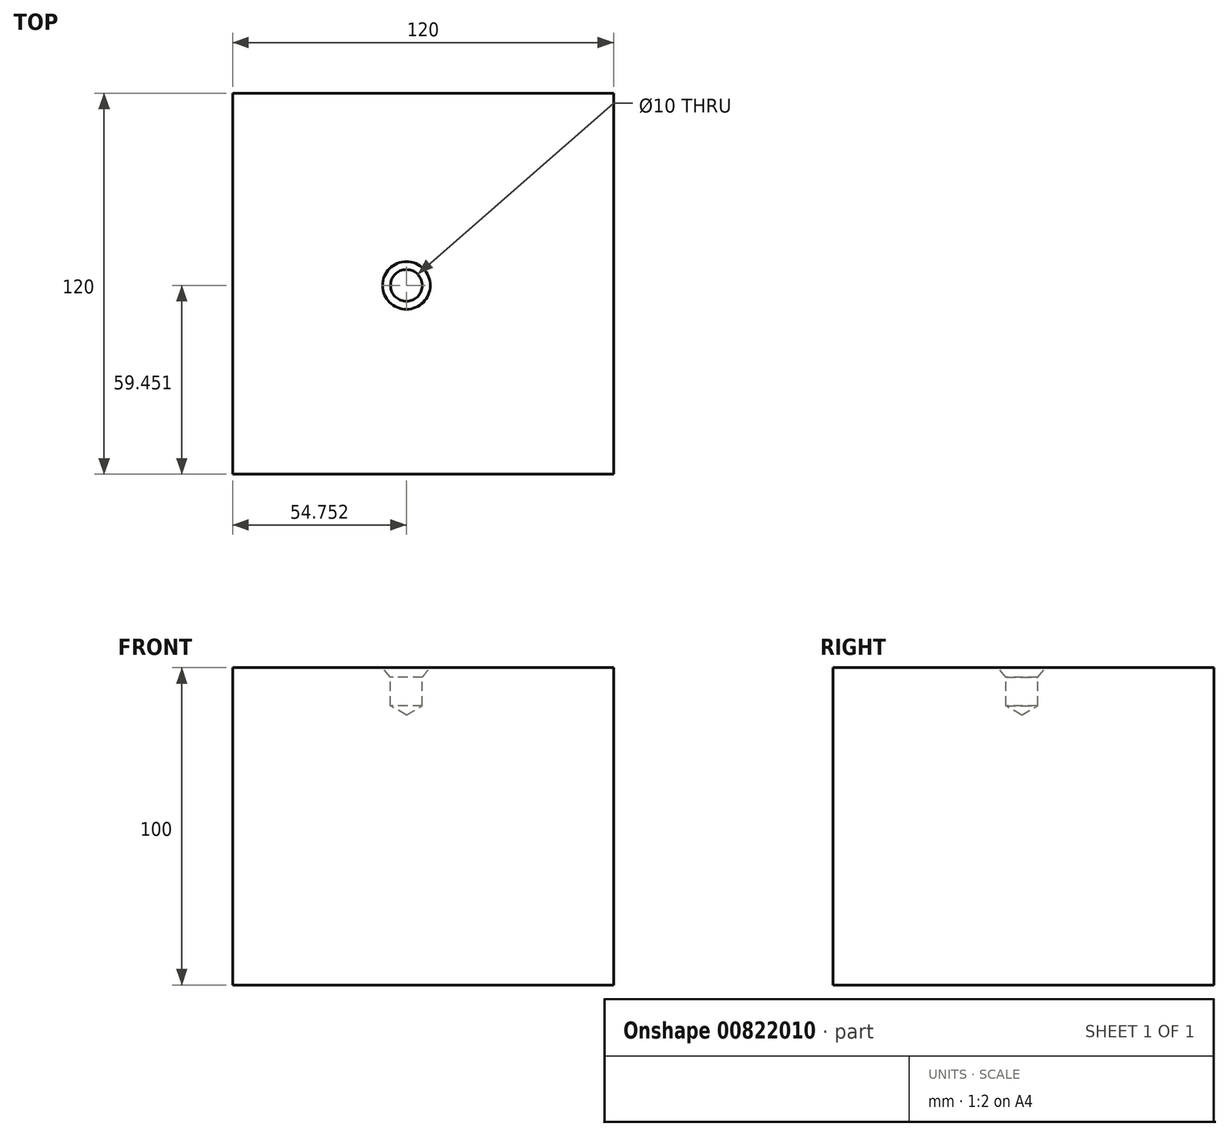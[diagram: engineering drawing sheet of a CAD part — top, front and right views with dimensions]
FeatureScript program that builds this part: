
annotation { "Feature Type Name" : "Feature", "Feature Type Description" : "" }
export const myFeature = defineFeature(function(context is Context, id is Id, definition is map)
    precondition{}
    {
        {
            var Q0;
            Q0=qCreatedBy(makeId("Top.planeOp"),FACE);
            var sketch = newSketch(context, id + "F0", { "sketchPlane" : qUnion([Q0])});
            skLineSegment(sketch, "E0.bottom", {"start": v(-65.58, -51.94) * mm, "end": v(54.42, -51.94) * mm});
            skLineSegment(sketch, "E0.top", {"start": v(-65.58, 68.06) * mm, "end": v(54.42, 68.06) * mm});
            skLineSegment(sketch, "E0.left", {"start": v(-65.58, -51.94) * mm, "end": v(-65.58, 68.06) * mm});
            skLineSegment(sketch, "E0.right", {"start": v(54.42, -51.94) * mm, "end": v(54.42, 68.06) * mm});
            skSolve(sketch);
        }
        {
            var Q0;
            Q0 = qSketchRegion(id + "F0", true);
            extrude(context, id + "F1", {"entities" : qUnion([Q0]), "depth" : 100 * mm, "offsetDistance" : 25 * mm});
        }
        {
            var Q0;
            Q0=makeQuery(id+"F1.opExtrude","CAP_FACE",FACE,{"disambiguationData":[OSD([sQuery(id+"F0.wireOp",EDGE,"E0.bottom"),sQuery(id+"F0.wireOp",EDGE,"E0.top"),sQuery(id+"F0.wireOp",EDGE,"E0.left"),sQuery(id+"F0.wireOp",EDGE,"E0.right")])],"isStart":false});
            var sketch = newSketch(context, id + "F2", { "sketchPlane" : qUnion([Q0])});
            skPoint(sketch, "E1", {"position": v(-10.83, 7.51) * mm});
            skSolve(sketch);
        }
        {
            var Q0;
            Q0=sQuery(id+"F2.wireOp",VERTEX,"E1");
            var Q1;
            Q1=makeQuery(id+"F1.opExtrude","SWEPT_BODY",BODY,{"disambiguationData":[OSD([sQuery(id+"F0.wireOp",EDGE,"E0.bottom"),sQuery(id+"F0.wireOp",EDGE,"E0.top"),sQuery(id+"F0.wireOp",EDGE,"E0.left"),sQuery(id+"F0.wireOp",EDGE,"E0.right")])]});
            hole(context, id + "F3", {"style" : HoleStyle.C_SINK, "endStyle" : HoleEndStyle.BLIND, "holeDiameter" : 10 * mm, "cSinkDiameter" : 15 * mm, "cSinkAngle" : 80 * degree, "majorDiameter" : 5 * mm, "holeDepth" : 12 * mm, "isTappedThrough" : true, "tappedDepth" : 12 * mm, "tapClearance" : 3, "locations" : qUnion([Q0]), "scope" : qUnion([Q1])});
        }
    });
